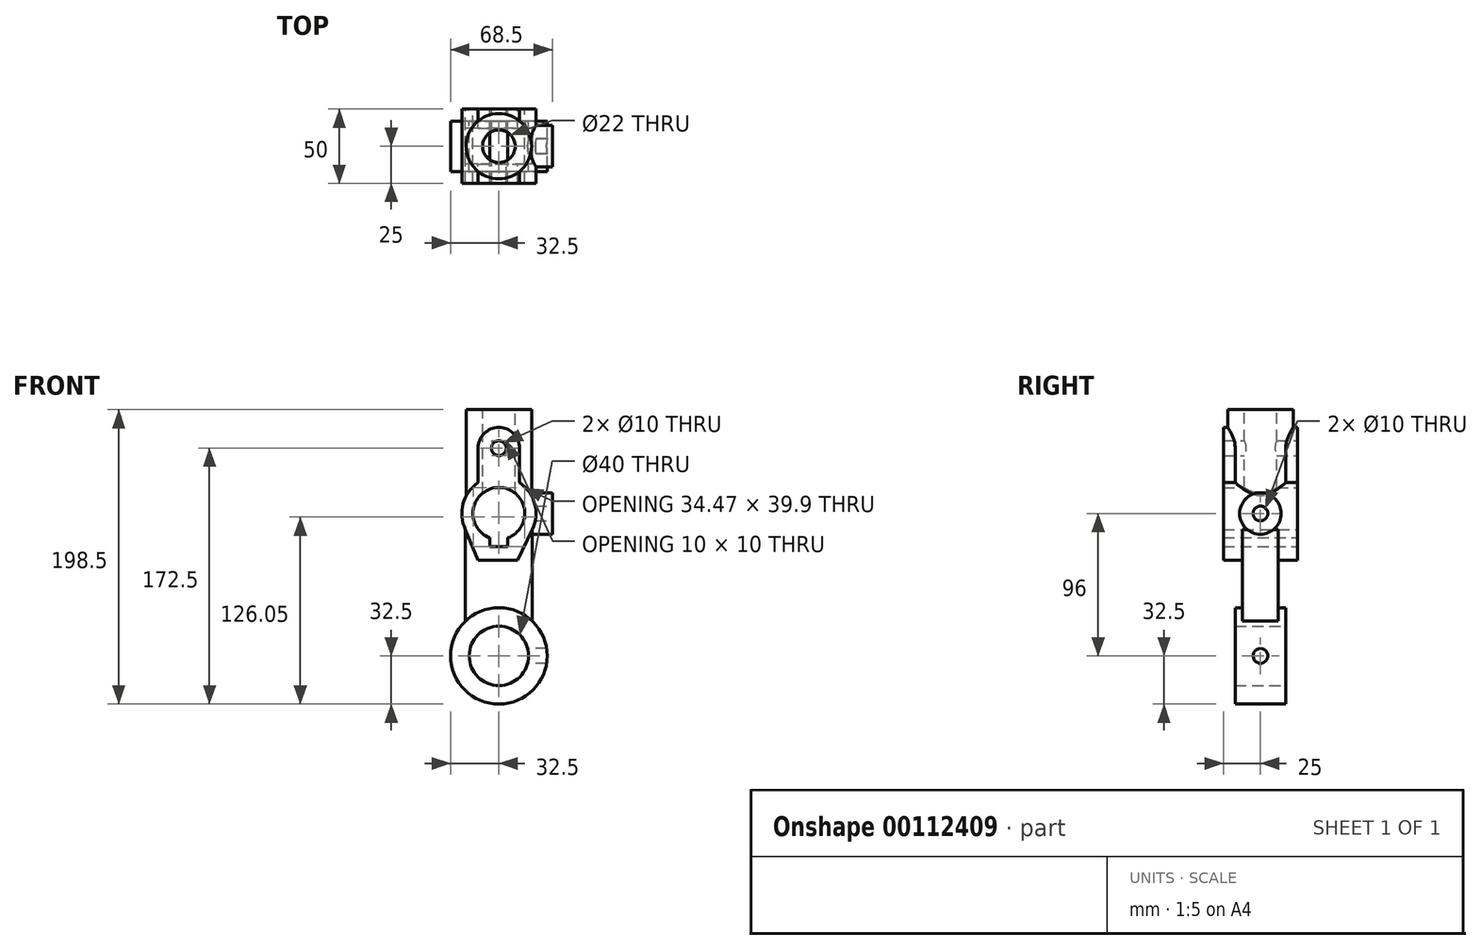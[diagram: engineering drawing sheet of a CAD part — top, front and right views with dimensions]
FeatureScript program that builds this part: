
annotation { "Feature Type Name" : "Feature", "Feature Type Description" : "" }
export const myFeature = defineFeature(function(context is Context, id is Id, definition is map)
    precondition{}
    {
        {
            var Q0;
            Q0=qCreatedBy(makeId("Front.planeOp"),FACE);
            var sketch = newSketch(context, id + "F0", { "sketchPlane" : qUnion([Q0])});
            skCircle(sketch, "E0", {"center": v(0, 0) * mm, "radius": 20 * mm});
            skCircle(sketch, "E1", {"center": v(0, 0) * mm, "radius": 32.5 * mm});
            skLineSegment(sketch, "E2", {"start": v(-22.5, 23.45) * mm, "end": v(-22.5, 85.1) * mm});
            skLineSegment(sketch, "E3", {"start": v(22.5, 23.45) * mm, "end": v(22.5, 85.1) * mm});
            skLineSegment(sketch, "E4", {"start": v(-14, 64.46) * mm, "end": v(12.5, 64.46) * mm});
            skLineSegment(sketch, "E5", {"start": v(-6, 73.6) * mm, "end": v(6, 73.6) * mm});
            skLineSegment(sketch, "E6", {"start": v(6, 73.6) * mm, "end": v(6, 79.56) * mm});
            skLineSegment(sketch, "E7", {"start": v(-6, 73.6) * mm, "end": v(-6, 79.56) * mm});
            skArc(sketch, "E8", {"start": v(6, 79.56) * mm, "mid": v(0, 113.5) * mm, "end": v(-6, 79.56) * mm});
            skLineSegment(sketch, "E9", {"start": v(14, 116.71) * mm, "end": v(14, 140) * mm});
            skLineSegment(sketch, "E10", {"start": v(-14, 116.71) * mm, "end": v(-14, 140) * mm});
            skArc(sketch, "E11", {"start": v(14, 140) * mm, "mid": v(0, 154) * mm, "end": v(-14, 140) * mm});
            skLineSegment(sketch, "E12", {"start": v(-14, 64.46) * mm, "end": v(-22.5, 85.1) * mm});
            skLineSegment(sketch, "E13", {"start": v(12.5, 64.46) * mm, "end": v(22.5, 85.1) * mm});
            skArc(sketch, "E14", {"start": v(-14, 116.71) * mm, "mid": v(-24.14, 102.5) * mm, "end": v(-22.5, 85.1) * mm});
            skArc(sketch, "E15", {"start": v(22.5, 85.1) * mm, "mid": v(24.14, 102.5) * mm, "end": v(14, 116.71) * mm});
            skCircle(sketch, "E16", {"center": v(0, 140) * mm, "radius": 5 * mm});
            skSolve(sketch);
        }
        {
            var Q0;
            Q0=makeQuery(id+"F0.imprint","IMPRINT",FACE,{"disambiguationData":[TD([[makeQuery(id+"F0.imprint","IMPRINT",EDGE,{"derivedFrom":sQuery(id+"F0.wireOp",EDGE,"E0")}),-1.0]])]});
            extrude(context, id + "F1", {"entities" : qUnion([Q0]), "endBound" : BoundingType.SYMMETRIC, "depth" : 34 * mm});
        }
        {
            var Q0;
            {var subQ1=sQuery(id+"F0.wireOp",EDGE,"E2");Q0=makeQuery(id+"F0.imprint","IMPRINT",FACE,{"disambiguationData":[TD([[makeQuery(id+"F0.imprint","IMPRINT",EDGE,{"derivedFrom":subQ1}),-1.0]])]});}
            extrude(context, id + "F2", {"entities" : qUnion([Q0]), "operationType" : NewBodyOperationType.ADD, "endBound" : BoundingType.SYMMETRIC, "depth" : 24 * mm});
        }
        {
            var Q0;
            Q0=makeQuery(id+"F0.imprint","IMPRINT",FACE,{"disambiguationData":[TD([[makeQuery(id+"F0.imprint","IMPRINT",EDGE,{"derivedFrom":sQuery(id+"F0.wireOp",EDGE,"E4")}),1.0]])]});
            extrude(context, id + "F3", {"entities" : qUnion([Q0]), "operationType" : NewBodyOperationType.ADD, "endBound" : BoundingType.SYMMETRIC, "depth" : 50 * mm});
        }
        {
            var Q0;
            Q0=qCreatedBy(makeId("Top.planeOp"),FACE);
            cPlane(context, id + "F4", {"entities" : qUnion([Q0]), "cplaneType" : CPlaneType.OFFSET, "offset" : 166 * mm, "width" : 150 * mm, "height" : 150 * mm});
        }
        {
            var Q0;
            Q0=qCreatedBy(id+"F4.planeOp",FACE);
            var sketch = newSketch(context, id + "F5", { "sketchPlane" : qUnion([Q0])});
            skCircle(sketch, "E17", {"center": v(0, 0) * mm, "radius": 11 * mm});
            skCircle(sketch, "E18", {"center": v(0, 0) * mm, "radius": 22 * mm});
            skSolve(sketch);
        }
        {
            var Q0;
            Q0=qCreatedBy(makeId("Right.planeOp"),FACE);
            var sketch = newSketch(context, id + "F6", { "sketchPlane" : qUnion([Q0])});
            skCircle(sketch, "E19", {"center": v(0, 0) * mm, "radius": 5 * mm});
            skCircle(sketch, "E20", {"center": v(0, 96) * mm, "radius": 5 * mm});
            skCircle(sketch, "E21", {"center": v(0, 96) * mm, "radius": 14 * mm});
            skSolve(sketch);
        }
        {
            var Q0;
            Q0=makeQuery(id+"F5.imprint","IMPRINT",FACE,{"disambiguationData":[TD([[makeQuery(id+"F5.imprint","IMPRINT",EDGE,{"derivedFrom":sQuery(id+"F5.wireOp",EDGE,"E17")}),-1.0]])]});
            extrude(context, id + "F7", {"entities" : qUnion([Q0]), "operationType" : NewBodyOperationType.ADD, "endBound" : BoundingType.UP_TO_NEXT, "oppositeDirection" : true, "depth" : 25 * mm});
        }
        {
            var Q0;
            Q0=makeQuery(id+"F6.imprint","IMPRINT",FACE,{"disambiguationData":[TD([[makeQuery(id+"F6.imprint","IMPRINT",EDGE,{"derivedFrom":sQuery(id+"F6.wireOp",EDGE,"E19")}),1.0]])]});
            var Q1;
            Q1=sQuery(id+"F6.wireOp",EDGE,"E19");
            extrude(context, id + "F8", {"entities" : qUnion([Q0]), "operationType" : NewBodyOperationType.REMOVE, "surfaceEntities" : qUnion([Q1]), "endBound" : BoundingType.THROUGH_ALL, "depth" : 25 * mm});
        }
        {
            var Q0;
            Q0=makeQuery(id+"F5.imprint","IMPRINT",FACE,{"disambiguationData":[TD([[makeQuery(id+"F5.imprint","IMPRINT",EDGE,{"derivedFrom":sQuery(id+"F5.wireOp",EDGE,"E17")}),1.0]])]});
            var Q1;
            Q1=makeQuery(id+"F3.opExtrude","SWEPT_FACE",FACE,{"disambiguationData":[OSD([sQuery(id+"F0.wireOp",EDGE,"E8")])]});
            extrude(context, id + "F9", {"entities" : qUnion([Q0]), "operationType" : NewBodyOperationType.REMOVE, "endBound" : BoundingType.UP_TO_SURFACE, "oppositeDirection" : true, "endBoundEntityFace" : qUnion([Q1]), "depth" : 25 * mm});
        }
        {
            var Q0;
            Q0=qCreatedBy(makeId("Right.planeOp"),FACE);
            cPlane(context, id + "F10", {"entities" : qUnion([Q0]), "cplaneType" : CPlaneType.OFFSET, "offset" : 36 * mm, "width" : 150 * mm, "height" : 150 * mm});
        }
        {
            var Q0;
            Q0=qCreatedBy(id+"F10.planeOp",FACE);
            var sketch = newSketch(context, id + "F11", { "sketchPlane" : qUnion([Q0])});
            skPoint(sketch, "E22.0", {"position": v(0, 96) * mm});
            skCircle(sketch, "E22.1", {"center": v(0, 96) * mm, "radius": 5 * mm});
            skCircle(sketch, "E22.2", {"center": v(0, 96) * mm, "radius": 14 * mm});
            skSolve(sketch);
        }
        {
            var Q0;
            Q0=makeQuery(id+"F11.imprint","IMPRINT",FACE,{"disambiguationData":[TD([[makeQuery(id+"F11.imprint","IMPRINT",EDGE,{"derivedFrom":sQuery(id+"F11.wireOp",EDGE,"E22.1")}),-1.0]])]});
            extrude(context, id + "F12", {"entities" : qUnion([Q0]), "operationType" : NewBodyOperationType.ADD, "endBound" : BoundingType.UP_TO_NEXT, "oppositeDirection" : true, "depth" : 25 * mm});
        }
    });
